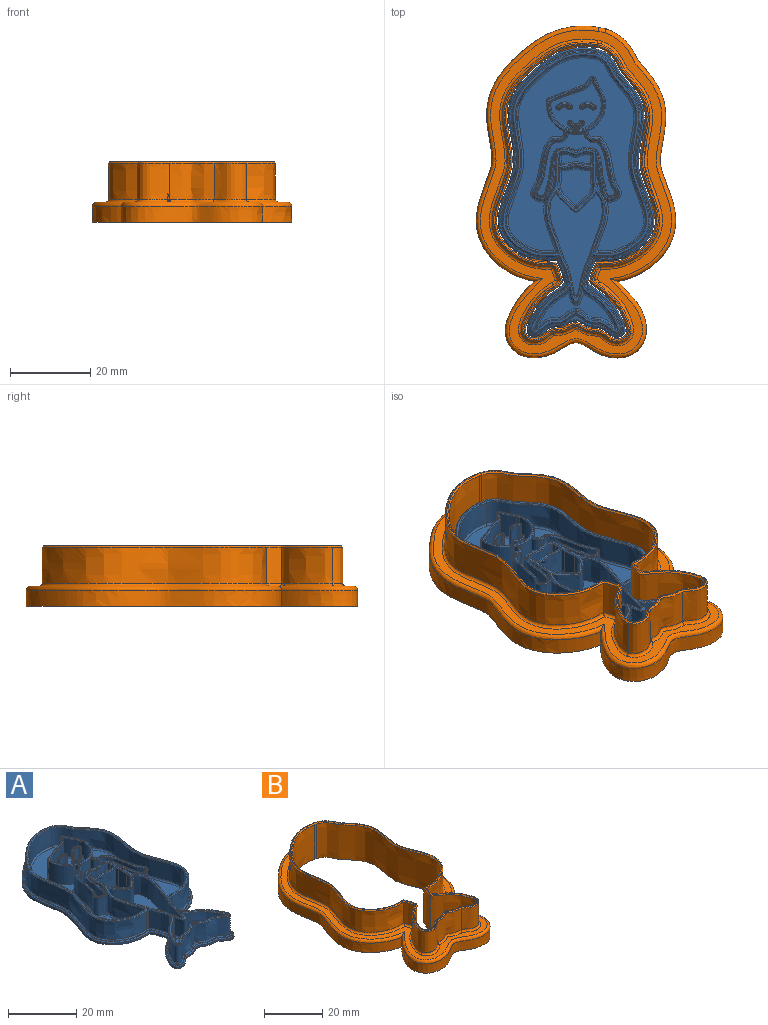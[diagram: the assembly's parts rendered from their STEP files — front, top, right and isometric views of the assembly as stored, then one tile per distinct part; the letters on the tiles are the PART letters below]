
ASSEMBLY  parts=2 mates=1
PART A: 305 faces, bbox 39.4x72.6x8.6 mm
  f0: plane 70.17x36.96mm, normal (0,0,1), area 142.6mm2, adj f242,f245,f246,f251,f252,f257,f262,f263
  f1: plane 12.52x11.75mm, normal (0,0,1), area 76.7mm2, adj f139,f140,f141,f142,f145,f146,f147,f148
  f2: plane 71.4x38.2mm, normal (0,0,1), area 60.9mm2, adj f98,f100,f101,f102,f103,f104,f105,f106
  f3: extruded ~5.41x1.93mm, area 3.7mm2, adj f4,f8,f9,f112
  f4: extruded ~52.46x14.48mm, area 43.8mm2, adj f3,f5,f9,f114
  f5: plane 0.65x0.51mm, normal (0.21,0.98,0), area 0.3mm2, adj f4,f6,f9,f115
  f6: extruded ~52.96x24.58mm, area 50.2mm2, adj f5,f7,f9,f113
  f7: extruded ~5.44x1.91mm, area 3.8mm2, adj f6,f8,f9,f111
  f8: extruded ~24.23x13.75mm, area 38.4mm2, adj f3,f7,f9,f110
  f9: plane 72.05x38.76mm, normal (0,0,-1), area 1871mm2, adj f3,f4,f5,f6,f7,f8
  f10: extruded ~6.25x3.82mm, area 54mm2, adj f11,f75,f123,f304
  f11: extruded ~6.25x1.11mm, area 8.5mm2, adj f10,f12,f121,f303
  f12: extruded ~20.45x9mm, area 320.2mm2, adj f11,f75,f116,f117,f118,f119,f120,f301
  f13: extruded ~9.98x6.75mm, area 96mm2, adj f68,f82,f288
  f14: extruded ~8.21x6.25mm, area 52.4mm2, adj f15,f69,f131,f286
  f15: plane 6.25x1mm, normal (-1,0,0), area 6.3mm2, adj f14,f16,f129,f287
  f16: extruded ~6.25x3.42mm, area 21.4mm2, adj f15,f17,f127,f285
  f17: extruded ~8.51x6.25mm, area 91.1mm2, adj f16,f18,f124,f125,f126,f283
  f18: extruded ~6.25x3.52mm, area 22mm2, adj f17,f69,f128,f282
  f19: extruded ~8.22x6.25mm, area 52.2mm2, adj f20,f70,f136,f277
  f20: extruded ~6.25x2.57mm, area 16.1mm2, adj f19,f21,f135,f278
  f21: extruded ~8.42x6.25mm, area 55.2mm2, adj f20,f22,f133,f280
  f22: extruded ~6.25x1.16mm, area 7.3mm2, adj f21,f70,f132,f281
  f23: cylinder r=7.36mm len=6.45mm, axis (0,0,-1), area 30.8mm2, adj f24,f71,f186,f255
  f24: extruded ~6.45x2.13mm, area 16.7mm2, adj f23,f25,f184,f260
  f25: plane 6.45x0.56mm, normal (-0.36,-0.93,0), area 3.9mm2, adj f24,f26,f182,f264
  f26: extruded ~13.82x6.45mm, area 114.8mm2, adj f25,f27,f180,f268
  f27: extruded ~6.45x0.57mm, area 4.2mm2, adj f26,f28,f178,f272
  f28: extruded ~10.59x6.45mm, area 71mm2, adj f27,f176,f204,f276
  f29: extruded ~8.97x6.45mm, area 60.4mm2, adj f173,f201,f204,f271
  f30: extruded ~10.56x6.45mm, area 70.8mm2, adj f31,f177,f201,f263
  f31: extruded ~6.45x0.61mm, area 4.4mm2, adj f30,f32,f179,f259
  f32: extruded ~13.82x6.45mm, area 114.7mm2, adj f31,f33,f181,f254
  f33: plane 6.45x0.56mm, normal (0.36,-0.93,0), area 3.9mm2, adj f32,f71,f183,f248
  f34: extruded ~6.75x0.44mm, area 3mm2, adj f72,f78,f207,f234
  f35: cylinder r=7.36mm len=7.47mm, axis (0,0,-1), area 61.4mm2, adj f36,f78,f207,f243
  f36: extruded ~6.75x1.9mm, area 15.2mm2, adj f35,f37,f78,f194,f247
  f37: extruded ~15.41x6.73mm, area 124.5mm2, adj f36,f38,f194,f253
  f38: extruded ~10.1x6.25mm, area 69mm2, adj f37,f39,f196,f258
  f39: extruded ~6.74x3.04mm, area 19.8mm2, adj f38,f40,f196,f252
  f40: extruded ~6.74x3.26mm, area 21.6mm2, adj f39,f41,f196,f198,f246
  f41: extruded ~16.84x6.25mm, area 111.4mm2, adj f40,f42,f198,f242
  f42: extruded ~6.25x1.04mm, area 6.5mm2, adj f41,f43,f200,f245
  f43: extruded ~48.95x22.38mm, area 437.8mm2, adj f42,f44,f199,f251
  f44: extruded ~48.58x12.27mm, area 379.6mm2, adj f43,f45,f197,f257
  f45: extruded ~6.25x1.02mm, area 6.4mm2, adj f44,f46,f195,f262
  f46: extruded ~16.67x6.25mm, area 110.3mm2, adj f45,f47,f193,f266
  f47: extruded ~6.74x3.26mm, area 21.6mm2, adj f46,f48,f192,f193,f270
  f48: extruded ~6.74x3.04mm, area 19.8mm2, adj f47,f49,f192,f274
  f49: extruded ~10.1x6.25mm, area 69.1mm2, adj f48,f50,f192,f273
  f50: extruded ~15.41x6.73mm, area 124.5mm2, adj f49,f51,f191,f269
  f51: extruded ~6.75x1.9mm, area 15.2mm2, adj f50,f52,f78,f191,f265
  f52: cylinder r=7.36mm len=8.12mm, axis (0,0,-1), area 65.9mm2, adj f51,f53,f78,f261
  f53: extruded ~6.75x0.98mm, area 7.1mm2, adj f52,f54,f78,f256
  f54: extruded ~6.75x3.75mm, area 28.3mm2, adj f53,f78,f208,f250
  f55: cylinder r=6.56mm len=13.12mm, axis (0,0,-1), area 144.3mm2, adj f56,f73,f190,f236
  f56: extruded ~10.63x6.45mm, area 80.2mm2, adj f55,f57,f189,f240
  f57: extruded ~6.45x4.08mm, area 29.3mm2, adj f56,f73,f187,f239
  f58: extruded ~50.95x23.41mm, area 470.6mm2, adj f59,f74,f109,f295
  f59: extruded ~6.4x1.05mm, area 6.7mm2, adj f58,f60,f107,f297
  f60: extruded ~6.46x6.4mm, area 44mm2, adj f59,f61,f105,f299
  f61: plane 6.45x0.02mm, normal (-1,0,0), area 0mm2, adj f60,f62,f103,f105
  f62: extruded ~6.4x1.13mm, area 8.9mm2, adj f61,f63,f103,f298
  f63: extruded ~21.69x11.47mm, area 332.1mm2, adj f62,f64,f98,f99,f101,f296
  f64: extruded ~6.4x1.16mm, area 9mm2, adj f63,f65,f100,f294
  f65: extruded ~6.63x6.4mm, area 45.2mm2, adj f64,f66,f102,f292
  f66: extruded ~6.4x1.03mm, area 6.6mm2, adj f65,f67,f104,f290
  f67: extruded ~50.5x13.09mm, area 409.1mm2, adj f66,f74,f106,f291
  f68: extruded ~25.64x13.13mm, area 372.4mm2, adj f13,f82,f289
  f69: extruded ~6.25x1mm, area 6.2mm2, adj f14,f18,f130,f284
  f70: plane 6.25x1.42mm, normal (-1,0,0), area 8.9mm2, adj f19,f22,f134,f279
  f71: extruded ~6.45x2.13mm, area 16.7mm2, adj f23,f33,f185,f249
  f72: extruded ~9.24x6.75mm, area 71mm2, adj f34,f78,f209,f237
  f73: extruded ~6.45x0.8mm, area 5.6mm2, adj f55,f57,f188,f235
  f74: plane 6.4x0.39mm, normal (0.21,0.98,0), area 2.5mm2, adj f58,f67,f108,f293
  f75: extruded ~6.25x1.12mm, area 8.6mm2, adj f10,f12,f122,f302
  f76: plane 30.71x21.28mm, normal (0,0,1), area 34mm2, adj f234,f235,f236,f237,f238,f239,f240,f241
  f77: plane 18.66x7.91mm, normal (0,0,1), area 52.3mm2, adj f116,f119,f120,f121,f122,f123
  f78: plane 47.99x33.76mm, normal (0,0,1), area 643mm2, adj f34,f35,f36,f51,f52,f53,f54,f72
  f79: plane 19.34x15.39mm, normal (0,0,1), area 54.9mm2, adj f173,f174,f175,f176,f177,f178,f179,f180
  f80: plane 7.47x2.21mm, normal (0,0,1), area 12.8mm2, adj f132,f133,f134,f135,f136
  f81: plane 9.15x7.51mm, normal (0,0,1), area 51.6mm2, adj f125,f126,f127,f128,f129,f130,f131
  f82: plane 26.04x13.44mm, normal (0,0,1), area 171.7mm2, adj f13,f68
  f83: plane 6.45x0.19mm, normal (0.39,0.92,0), area 1.3mm2, adj f167,f168,f172,f232
  f84: cylinder r=1.38mm len=6.45mm, axis (0,0,-1), area 17.6mm2, adj f162,f168,f169,f228
  f85: plane 6.45x0.19mm, normal (-0.39,0.92,0), area 1.3mm2, adj f161,f162,f163,f227
  f86: cylinder r=2.18mm len=6.45mm, axis (0,0,-1), area 28.3mm2, adj f161,f166,f167,f231
  f87: plane 3.28x1.05mm, normal (0,0,1), area 1.1mm2, adj f226,f227,f228,f229,f230,f231,f232,f233
  f88: plane 6.45x0.17mm, normal (-0.57,-0.82,0), area 1.3mm2, adj f154,f157,f160,f215
  f89: cylinder r=1.53mm len=6.45mm, axis (0,0,-1), area 16.5mm2, adj f149,f154,f155,f216
  f90: plane 6.45x0.17mm, normal (0.51,-0.86,0), area 1.3mm2, adj f149,f150,f151,f212
  f91: cylinder r=2.33mm len=6.45mm, axis (0,0,-1), area 25.7mm2, adj f151,f156,f157,f211
  f92: plane 3.16x0.95mm, normal (0,0,1), area 1mm2, adj f210,f211,f212,f213,f214,f215,f216,f217
  f93: cylinder r=1.53mm len=6.45mm, axis (0,0,-1), area 16.5mm2, adj f143,f144,f148,f224
  f94: plane 6.45x0.17mm, normal (0.57,-0.82,0), area 1.3mm2, adj f138,f144,f145,f220
  f95: cylinder r=2.33mm len=6.45mm, axis (0,0,-1), area 25.7mm2, adj f137,f138,f139,f219
  f96: plane 6.45x0.17mm, normal (-0.51,-0.86,0), area 1.3mm2, adj f137,f142,f143,f223
  f97: plane 3.16x0.95mm, normal (0,0,1), area 1mm2, adj f218,f219,f220,f221,f222,f223,f224,f225
  f98: bspline ~12x11.61mm, area 14.7mm2, adj f2,f63,f99,f100
  f99: bspline ~0.35x0.35mm, area 0mm2, adj f63,f98,f101
  f100: bspline ~1.71x1.28mm, area 0.7mm2, adj f2,f64,f98,f102
  f101: bspline ~12x11.61mm, area 15mm2, adj f2,f63,f99,f103
  f102: bspline ~7.49x2.86mm, area 3.7mm2, adj f2,f65,f100,f104
  f103: bspline ~1.89x1.5mm, area 0.7mm2, adj f2,f61,f62,f101,f105
  f104: bspline ~1.51x0.47mm, area 0.5mm2, adj f2,f66,f102,f106
  f105: bspline ~7.79x3mm, area 3.7mm2, adj f2,f60,f61,f103,f107
  f106: bspline ~51.37x27.17mm, area 35.3mm2, adj f2,f67,f104,f108
  f107: bspline ~1.49x0.41mm, area 0.5mm2, adj f2,f59,f105,f109
  f108: cylinder r=0.35mm len=0.5mm, axis (0.98,-0.21,0), area 0.2mm2, adj f2,f74,f106,f109
  f109: bspline ~51.69x25.19mm, area 40.7mm2, adj f2,f58,f107,f108
  f110: bspline ~24.34x14.17mm, area 32.3mm2, adj f2,f8,f111,f112
  f111: bspline ~7.78x3.04mm, area 3.3mm2, adj f2,f7,f110,f113
  f112: bspline ~7.02x2.7mm, area 3.3mm2, adj f2,f3,f110,f114
  f113: bspline ~52.99x25.08mm, area 42.3mm2, adj f2,f6,f111,f115
  f114: bspline ~52.57x15.23mm, area 36.7mm2, adj f2,f4,f112,f115
  f115: cylinder r=0.35mm len=0.58mm, axis (0.98,-0.21,0), area 0.3mm2, adj f2,f5,f113,f114
  f116: bspline ~20.48x5.28mm, area 17mm2, adj f12,f77,f117,f118
  f117: bspline ~1.14x0.93mm, area 0.3mm2, adj f12,f116,f119
  f118: bspline ~1.14x0.93mm, area 0.4mm2, adj f12,f116,f120
  f119: bspline ~9.42x8.61mm, area 9mm2, adj f12,f77,f117,f121
  f120: bspline ~9.3x8.39mm, area 9mm2, adj f12,f77,f118,f122
  f121: bspline ~1.82x1.52mm, area 0.7mm2, adj f11,f77,f119,f123
  f122: bspline ~3.59x3.28mm, area 0.7mm2, adj f75,f77,f120,f123
  f123: bspline ~5.07x4.45mm, area 6.3mm2, adj f10,f77,f121,f122
  f124: bspline ~0.59x0.5mm, area 0.1mm2, adj f17,f125,f126
  f125: bspline ~6.93x4.44mm, area 5.3mm2, adj f17,f81,f124,f127
  f126: bspline ~5.64x4.48mm, area 5.3mm2, adj f17,f81,f124,f128
  f127: bspline ~4.71x0.66mm, area 2.7mm2, adj f16,f81,f125,f129
  f128: bspline ~4.88x0.66mm, area 2.8mm2, adj f18,f81,f126,f130
  f129: cylinder r=0.5mm len=1mm, axis (0,1,0), area 0.5mm2, adj f15,f81,f127,f131
  f130: bspline ~1.26x0.51mm, area 0.5mm2, adj f69,f81,f128,f131
  f131: bspline ~8.99x1.05mm, area 6.2mm2, adj f14,f81,f129,f130
  f132: bspline ~1.76x0.7mm, area 0.8mm2, adj f22,f80,f133,f134
  f133: bspline ~8.83x1.25mm, area 6.6mm2, adj f21,f80,f132,f135
  f134: cylinder r=0.5mm len=1.48mm, axis (0,1,0), area 1mm2, adj f70,f80,f132,f136
  f135: bspline ~2.82x0.65mm, area 1.7mm2, adj f20,f80,f133,f136
  f136: bspline ~9.17x0.96mm, area 6.2mm2, adj f19,f80,f134,f135
  f137: cylinder r=0.3mm len=6.45mm, axis (0,0,-1), area 3.3mm2, adj f95,f96,f140,f221
  f138: cylinder r=0.3mm len=6.45mm, axis (0,0,-1), area 3.3mm2, adj f94,f95,f141,f218
  f139: torus R=2.63mm, axis (0,0,1), area 2mm2, adj f1,f95,f140,f141
  f140: torus R=0.6mm, axis (0,0,1), area 0.3mm2, adj f1,f137,f139,f142
  f141: torus R=0.6mm, axis (0,0,1), area 0.3mm2, adj f1,f138,f139,f145
  f142: cylinder r=0.3mm len=0.36mm, axis (-0.86,0.51,0), area 0.1mm2, adj f1,f96,f140,f146
  f143: cylinder r=0.3mm len=6.45mm, axis (0,0,-1), area 2.7mm2, adj f93,f96,f146,f225
  f144: cylinder r=0.3mm len=6.45mm, axis (0,0,-1), area 2.7mm2, adj f93,f94,f147,f222
  f145: cylinder r=0.3mm len=0.36mm, axis (-0.82,-0.57,0), area 0.1mm2, adj f1,f94,f141,f147
  f146: torus R=0.6mm, axis (0,0,1), area 0.3mm2, adj f1,f142,f143,f148
  f147: torus R=0.6mm, axis (0,0,1), area 0.3mm2, adj f1,f144,f145,f148
  f148: torus R=1.23mm, axis (0,0,1), area 1.1mm2, adj f1,f93,f146,f147
  f149: cylinder r=0.3mm len=6.45mm, axis (0,0,-1), area 2.7mm2, adj f89,f90,f152,f214
  f150: cylinder r=0.3mm len=0.36mm, axis (-0.86,-0.51,0), area 0.1mm2, adj f1,f90,f152,f153
  f151: cylinder r=0.3mm len=6.45mm, axis (0,0,-1), area 3.3mm2, adj f90,f91,f153,f210
  f152: torus R=0.6mm, axis (0,0,1), area 0.3mm2, adj f1,f149,f150,f155
  f153: torus R=0.6mm, axis (0,0,1), area 0.3mm2, adj f1,f150,f151,f156
  f154: cylinder r=0.3mm len=6.45mm, axis (0,0,-1), area 2.7mm2, adj f88,f89,f158,f217
  f155: torus R=1.23mm, axis (0,0,1), area 1.1mm2, adj f1,f89,f152,f158
  f156: torus R=2.63mm, axis (0,0,1), area 2mm2, adj f1,f91,f153,f159
  f157: cylinder r=0.3mm len=6.45mm, axis (0,0,-1), area 3.3mm2, adj f88,f91,f159,f213
  f158: torus R=0.6mm, axis (0,0,1), area 0.3mm2, adj f1,f154,f155,f160
  f159: torus R=0.6mm, axis (0,0,1), area 0.3mm2, adj f1,f156,f157,f160
  f160: cylinder r=0.3mm len=0.36mm, axis (-0.82,0.57,0), area 0.1mm2, adj f1,f88,f158,f159
  f161: cylinder r=0.3mm len=6.45mm, axis (0,0,-1), area 3.3mm2, adj f85,f86,f164,f229
  f162: cylinder r=0.3mm len=6.45mm, axis (0,0,-1), area 2.7mm2, adj f84,f85,f165,f226
  f163: cylinder r=0.3mm len=0.36mm, axis (0.92,0.39,0), area 0.1mm2, adj f1,f85,f164,f165
  f164: torus R=0.6mm, axis (0,0,1), area 0.3mm2, adj f1,f161,f163,f166
  f165: torus R=0.6mm, axis (0,0,1), area 0.3mm2, adj f1,f162,f163,f169
  f166: torus R=2.48mm, axis (0,0,1), area 2.2mm2, adj f1,f86,f164,f170
  f167: cylinder r=0.3mm len=6.45mm, axis (0,0,-1), area 3.3mm2, adj f83,f86,f170,f233
  f168: cylinder r=0.3mm len=6.45mm, axis (0,0,-1), area 2.7mm2, adj f83,f84,f171,f230
  f169: torus R=1.08mm, axis (0,0,1), area 1.2mm2, adj f1,f84,f165,f171
  f170: torus R=0.6mm, axis (0,0,1), area 0.3mm2, adj f1,f166,f167,f172
  f171: torus R=0.6mm, axis (0,0,1), area 0.3mm2, adj f1,f168,f169,f172
  f172: cylinder r=0.3mm len=0.36mm, axis (0.92,-0.39,0), area 0.1mm2, adj f1,f83,f170,f171
  f173: bspline ~9.92x1.06mm, area 4.4mm2, adj f29,f79,f174,f175,f203,f205
  f174: cylinder r=0.3mm len=0.2mm, axis (1,0,0), area 0mm2, adj f79,f173,f206
  f175: cylinder r=0.3mm len=0.2mm, axis (1,0,0), area 0mm2, adj f79,f173,f202
  f176: bspline ~13.6x4.17mm, area 5.3mm2, adj f28,f79,f178,f205,f206
  f177: bspline ~20.63x6.61mm, area 5.3mm2, adj f30,f79,f179,f202,f203
  f178: bspline ~1.05x0.75mm, area 0.3mm2, adj f27,f79,f176,f180
  f179: bspline ~0.87x0.65mm, area 0.3mm2, adj f31,f79,f177,f181
  f180: bspline ~13.83x6.11mm, area 8.2mm2, adj f26,f79,f178,f182
  f181: bspline ~13.82x6.45mm, area 8.2mm2, adj f32,f79,f179,f183
  f182: cylinder r=0.3mm len=0.77mm, axis (-0.93,0.36,0), area 0.3mm2, adj f25,f79,f180,f184
  f183: cylinder r=0.3mm len=0.77mm, axis (-0.93,-0.36,0), area 0.3mm2, adj f33,f79,f181,f185
  f184: bspline ~3.32x2.33mm, area 1.2mm2, adj f24,f79,f182,f186
  f185: bspline ~3.32x2.33mm, area 1.2mm2, adj f71,f79,f183,f186
  f186: torus R=7.66mm, axis (0,0,1), area 2.1mm2, adj f23,f79,f184,f185
  f187: bspline ~5.63x2.91mm, area 2mm2, adj f1,f57,f188,f189
  f188: bspline ~1.44x0.79mm, area 0.4mm2, adj f1,f73,f187,f190
  f189: bspline ~11.14x6.3mm, area 5.7mm2, adj f1,f56,f187,f190
  f190: torus R=6.26mm, axis (0,0,1), area 10.3mm2, adj f1,f55,f188,f189
  f191: bspline ~16.42x8.43mm, area 16.3mm2, adj f50,f51,f78,f192
  f192: bspline ~10.92x5.57mm, area 6.2mm2, adj f47,f48,f49,f78,f191,f193
  f193: bspline ~30.74x5.23mm, area 14.7mm2, adj f46,f47,f78,f192,f195
  f194: bspline ~16.44x9.14mm, area 16.3mm2, adj f36,f37,f78,f196
  f195: bspline ~1.36x0.6mm, area 0.6mm2, adj f45,f78,f193,f197
  f196: bspline ~10.95x5.58mm, area 6.2mm2, adj f38,f39,f40,f78,f194,f198
  f197: bspline ~48.66x25.3mm, area 47.3mm2, adj f44,f78,f195,f199
  f198: bspline ~23.14x3.86mm, area 14.8mm2, adj f40,f41,f78,f196,f200
  f199: bspline ~48.99x22.66mm, area 54.5mm2, adj f43,f78,f197,f200
  f200: bspline ~1.49x0.55mm, area 0.6mm2, adj f42,f78,f198,f199
  f201: cylinder r=1mm len=6.45mm, axis (0,0,-1), area 3.4mm2, adj f29,f30,f203,f267
  f202: bspline ~0.36x0.3mm, area 0mm2, adj f175,f177,f203
  f203: bspline ~0.45x0.45mm, area 0.1mm2, adj f173,f177,f201,f202
  f204: cylinder r=1mm len=6.45mm, axis (0,0,-1), area 3.4mm2, adj f28,f29,f205,f275
  f205: bspline ~0.48x0.45mm, area 0.1mm2, adj f173,f176,f204,f206
  f206: bspline ~0.36x0.3mm, area 0mm2, adj f174,f176,f205
  f207: cylinder r=1mm len=6.75mm, axis (0,0,-1), area 9.2mm2, adj f34,f35,f78,f238
  f208: cylinder r=1mm len=6.75mm, axis (0,0,-1), area 9.4mm2, adj f54,f78,f209,f244
  f209: cylinder r=1mm len=6.75mm, axis (0,0,-1), area 5mm2, adj f72,f78,f208,f241
  f210: cone r=0.05mm half-angle=45deg, axis (0,0,-1), area 0.1mm2, adj f92,f151,f211,f212
  f211: cone r=2.08mm half-angle=45deg, axis (0,0,-1), area 1.3mm2, adj f91,f92,f210,f213
  f212: plane 0.32x0.3mm, normal (0.36,-0.61,0.71), area 0.1mm2, adj f90,f92,f210,f214
  f213: cone r=0.05mm half-angle=45deg, axis (0,0,-1), area 0.1mm2, adj f92,f157,f211,f215
  f214: cone r=0.05mm half-angle=45deg, axis (0,0,-1), area 0.1mm2, adj f92,f149,f212,f216
  f215: plane 0.32x0.31mm, normal (-0.4,-0.58,0.71), area 0.1mm2, adj f88,f92,f213,f217
  f216: cone r=1.53mm half-angle=45deg, axis (0,0,1), area 1mm2, adj f89,f92,f214,f217
  f217: cone r=0.05mm half-angle=45deg, axis (0,0,-1), area 0.1mm2, adj f92,f154,f215,f216
  f218: cone r=0.05mm half-angle=45deg, axis (0,0,-1), area 0.1mm2, adj f97,f138,f219,f220
  f219: cone r=2.08mm half-angle=45deg, axis (0,0,-1), area 1.3mm2, adj f95,f97,f218,f221
  f220: plane 0.32x0.31mm, normal (0.4,-0.58,0.71), area 0.1mm2, adj f94,f97,f218,f222
  f221: cone r=0.05mm half-angle=45deg, axis (0,0,-1), area 0.1mm2, adj f97,f137,f219,f223
  f222: cone r=0.05mm half-angle=45deg, axis (0,0,-1), area 0.1mm2, adj f97,f144,f220,f224
  f223: plane 0.32x0.3mm, normal (-0.36,-0.61,0.71), area 0.1mm2, adj f96,f97,f221,f225
  f224: cone r=1.53mm half-angle=45deg, axis (0,0,1), area 1mm2, adj f93,f97,f222,f225
  f225: cone r=0.05mm half-angle=45deg, axis (0,0,-1), area 0.1mm2, adj f97,f143,f223,f224
  f226: cone r=0.05mm half-angle=45deg, axis (0,0,-1), area 0.1mm2, adj f87,f162,f227,f228
  f227: plane 0.31x0.29mm, normal (-0.28,0.65,0.71), area 0.1mm2, adj f85,f87,f226,f229
  f228: cone r=1.38mm half-angle=45deg, axis (0,0,1), area 1.1mm2, adj f84,f87,f226,f230
  f229: cone r=0.05mm half-angle=45deg, axis (0,0,-1), area 0.1mm2, adj f87,f161,f227,f231
  f230: cone r=0.05mm half-angle=45deg, axis (0,0,-1), area 0.1mm2, adj f87,f168,f228,f232
  f231: cone r=1.93mm half-angle=45deg, axis (0,0,-1), area 1.5mm2, adj f86,f87,f229,f233
  f232: plane 0.31x0.29mm, normal (0.28,0.65,0.71), area 0.1mm2, adj f83,f87,f230,f233
  f233: cone r=0.05mm half-angle=45deg, axis (0,0,-1), area 0.1mm2, adj f87,f167,f231,f232
  f234: bspline ~0.54x0.33mm, area 0.2mm2, adj f34,f76,f237,f238
  f235: bspline ~0.95x0.58mm, area 0.3mm2, adj f73,f76,f236,f239
  f236: cone r=6.56mm half-angle=45deg, axis (0,0,1), area 8.1mm2, adj f55,f76,f235,f240
  f237: bspline ~9.96x5.01mm, area 3.7mm2, adj f72,f76,f234,f241
  f238: cone r=0.75mm half-angle=45deg, axis (0,0,-1), area 0.4mm2, adj f76,f207,f234,f243
  f239: bspline ~5.2x2.68mm, area 1.7mm2, adj f57,f76,f235,f240,f244
  f240: bspline ~11.79x7.55mm, area 4.5mm2, adj f56,f76,f236,f239,f244
  f241: cone r=0.75mm half-angle=45deg, axis (0,0,-1), area 0.2mm2, adj f76,f209,f237,f244
  f242: bspline ~18.52x3.64mm, area 6.3mm2, adj f0,f41,f245,f246
  f243: cone r=7.11mm half-angle=45deg, axis (0,0,-1), area 3.2mm2, adj f35,f76,f238,f247
  f244: cone r=0.75mm half-angle=45deg, axis (0,0,-1), area 0.4mm2, adj f76,f208,f239,f240,f241,f250
  f245: bspline ~1.37x0.3mm, area 0.4mm2, adj f0,f42,f242,f251
  f246: bspline ~3.45x0.42mm, area 1.2mm2, adj f0,f40,f242,f252
  f247: bspline ~2.54x1.33mm, area 0.9mm2, adj f36,f76,f243,f253
  f248: plane 0.62x0.44mm, normal (0.26,-0.66,0.71), area 0.2mm2, adj f33,f76,f249,f254
  f249: bspline ~2.76x1.42mm, area 0.9mm2, adj f71,f76,f248,f255
  f250: bspline ~4.05x2.19mm, area 1.5mm2, adj f54,f76,f244,f256
  f251: bspline ~49.53x23.17mm, area 25mm2, adj f0,f43,f245,f257
  f252: bspline ~5.19x0.29mm, area 1.4mm2, adj f0,f39,f246,f258
  f253: bspline ~15.47x7.4mm, area 6.9mm2, adj f37,f76,f247,f258
  f254: bspline ~14.35x6.74mm, area 6.5mm2, adj f32,f76,f248,f259
  f255: cone r=7.11mm half-angle=45deg, axis (0,0,-1), area 1.8mm2, adj f23,f76,f249,f260
  f256: bspline ~1.15x0.66mm, area 0.4mm2, adj f53,f76,f250,f261
  f257: bspline ~49.73x14.25mm, area 21.5mm2, adj f0,f44,f251,f262
  f258: bspline ~12.61x3.74mm, area 4.2mm2, adj f38,f76,f252,f253,f263
  f259: bspline ~0.77x0.55mm, area 0.3mm2, adj f31,f76,f254,f263
  f260: bspline ~2.76x1.42mm, area 0.9mm2, adj f24,f76,f255,f264
  f261: cone r=7.11mm half-angle=45deg, axis (0,0,-1), area 3.4mm2, adj f52,f76,f256,f265
  f262: bspline ~1.35x0.36mm, area 0.4mm2, adj f0,f45,f257,f266
  f263: bspline ~10.65x2.73mm, area 3.9mm2, adj f0,f30,f76,f258,f259,f267
  f264: plane 0.62x0.44mm, normal (-0.26,-0.66,0.71), area 0.2mm2, adj f25,f76,f260,f268
  f265: bspline ~2.54x1.33mm, area 0.9mm2, adj f51,f76,f261,f269
  f266: bspline ~18.33x3.58mm, area 6.3mm2, adj f0,f46,f262,f270
  f267: cone r=0.75mm half-angle=45deg, axis (0,0,-1), area 0.2mm2, adj f0,f201,f263,f271
  f268: bspline ~14.35x6.75mm, area 6.5mm2, adj f26,f76,f264,f272
  f269: bspline ~15.47x7.42mm, area 6.9mm2, adj f50,f76,f265,f273
  f270: bspline ~3.28x0.4mm, area 1.2mm2, adj f0,f47,f266,f274
  f271: bspline ~9.83x1.05mm, area 3.3mm2, adj f0,f29,f267,f275
  f272: bspline ~0.73x0.54mm, area 0.2mm2, adj f27,f76,f268,f276
  f273: bspline ~12.62x3.74mm, area 4.2mm2, adj f49,f76,f269,f274,f276
  f274: bspline ~5.2x0.29mm, area 1.4mm2, adj f0,f48,f270,f273
  f275: cone r=0.75mm half-angle=45deg, axis (0,0,-1), area 0.2mm2, adj f0,f204,f271,f276
  f276: bspline ~10.68x2.74mm, area 3.9mm2, adj f0,f28,f76,f272,f273,f275
  f277: bspline ~9.57x0.73mm, area 3mm2, adj f0,f19,f278,f279
  f278: bspline ~3.2x0.41mm, area 1mm2, adj f0,f20,f277,f280
  f279: plane 1.61x0.25mm, normal (-0.71,0,0.71), area 0.5mm2, adj f0,f70,f277,f281
  f280: bspline ~9.68x1.04mm, area 3.2mm2, adj f0,f21,f278,f281
  f281: bspline ~1.37x0.37mm, area 0.4mm2, adj f0,f22,f279,f280
  f282: bspline ~3.52x0.42mm, area 1.2mm2, adj f0,f18,f283,f284
  f283: bspline ~9.01x5.75mm, area 5.3mm2, adj f0,f17,f282,f285
  f284: bspline ~1.43x0.26mm, area 0.4mm2, adj f0,f69,f282,f286
  f285: bspline ~3.42x0.42mm, area 1.2mm2, adj f0,f16,f283,f287
  f286: bspline ~9.71x0.82mm, area 3.1mm2, adj f0,f14,f284,f287
  f287: plane 1.37x0.25mm, normal (-0.71,0,0.71), area 0.4mm2, adj f0,f15,f285,f286
  f288: bspline ~10.31x5.43mm, area 5.1mm2, adj f0,f13,f289
  f289: bspline ~27.91x13.69mm, area 19.5mm2, adj f0,f68,f288
  f290: bspline ~1.3x0.36mm, area 0.4mm2, adj f0,f66,f291,f292
  f291: bspline ~51.2x14.76mm, area 22.4mm2, adj f0,f67,f290,f293
  f292: bspline ~7.77x2.89mm, area 2.6mm2, adj f0,f65,f290,f294
  f293: plane 0.44x0.33mm, normal (0.15,0.69,0.71), area 0.1mm2, adj f0,f74,f291,f295
  f294: bspline ~1.43x1.11mm, area 0.5mm2, adj f0,f64,f292,f296
  f295: bspline ~51.03x23.93mm, area 25.9mm2, adj f0,f58,f293,f297
  f296: bspline ~22.59x11.51mm, area 20.3mm2, adj f0,f63,f294,f298
  f297: bspline ~1.24x0.3mm, area 0.4mm2, adj f0,f59,f295,f299
  f298: bspline ~1.38x1.08mm, area 0.5mm2, adj f0,f62,f296,f300
  f299: bspline ~7.42x2.79mm, area 2.5mm2, adj f0,f60,f297,f300
  f300: plane 0.25x0.25mm, normal (-0.71,0,0.71), area 0mm2, adj f0,f298,f299
  f301: bspline ~21.03x9.65mm, area 17.6mm2, adj f0,f12,f302,f303
  f302: bspline ~1.94x1.32mm, area 0.6mm2, adj f0,f75,f301,f304
  f303: bspline ~1.87x1.28mm, area 0.6mm2, adj f0,f11,f301,f304
  f304: bspline ~5.04x3.68mm, area 3.2mm2, adj f0,f10,f302,f303
PART B: 61 faces, bbox 50x83.5x15.4 mm
  f0: extruded ~11.81x8.9mm, area 132.2mm2, adj f1,f10,f31,f46
  f1: extruded ~8.9x1.17mm, area 13.6mm2, adj f0,f2,f30,f44
  f2: extruded ~8.9x3.68mm, area 34.8mm2, adj f1,f3,f32,f43
  f3: extruded ~55.75x26mm, area 720.7mm2, adj f2,f4,f34,f45
  f4: plane 8.9x0.87mm, normal (0.21,0.98,0), area 7.9mm2, adj f3,f5,f36,f47
  f5: extruded ~55.19x15.01mm, area 625.8mm2, adj f4,f6,f38,f49
  f6: extruded ~8.9x3.6mm, area 34.1mm2, adj f5,f7,f40,f50
  f7: extruded ~8.9x1.03mm, area 11.7mm2, adj f6,f8,f42,f52
  f8: extruded ~12.34x8.9mm, area 136.9mm2, adj f7,f9,f41,f54
  f9: extruded ~8.9x8.05mm, area 86.9mm2, adj f8,f11,f39,f53
  f10: extruded ~8.9x7.9mm, area 86.5mm2, adj f0,f12,f33,f48
  f11: extruded ~11.05x8.9mm, area 103.8mm2, adj f9,f12,f37,f51
  f12: plane 8.9x0mm, normal (0.2,-0.98,0), area 0mm2, adj f10,f11,f35
  f13: extruded ~14.65x4.9mm, area 76.5mm2, adj f14,f18,f20,f59
  f14: extruded ~53.24x14.65mm, area 999.5mm2, adj f13,f15,f20,f60
  f15: plane 14.65x0.61mm, normal (-0.21,-0.98,0), area 9.1mm2, adj f14,f16,f20,f58
  f16: extruded ~53.76x24.99mm, area 1146.1mm2, adj f15,f17,f20,f56
  f17: extruded ~14.65x4.95mm, area 77.1mm2, adj f16,f18,f20,f55
  f18: extruded ~25.07x14.65mm, area 878.3mm2, adj f13,f17,f20,f57
  f19: plane 74.57x41.4mm, normal (0,0,1), area 68.4mm2, adj f43,f44,f45,f46,f47,f48,f49,f50
  f20: plane 83.04x49.56mm, normal (0,0,-1), area 1141.3mm2, adj f13,f14,f15,f16,f17,f18,f21,f22
  f21: extruded ~35.01x19.03mm, area 293.6mm2, adj f20,f22,f24,f29
  f22: extruded ~63.47x30.38mm, area 354.9mm2, adj f20,f21,f23,f28
  f23: plane 4x1.88mm, normal (0.21,0.98,0), area 7.7mm2, adj f20,f22,f24,f26
  f24: extruded ~62.73x17.21mm, area 305.2mm2, adj f20,f21,f23,f27
  f25: plane 80.55x47.57mm, normal (0,0,1), area 514.9mm2, adj f26,f27,f28,f29,f30,f31,f32,f33
  f26: cylinder r=1mm len=2.09mm, axis (-0.98,0.21,0), area 2.9mm2, adj f23,f25,f27,f28
  f27: bspline ~63.18x17.93mm, area 120.2mm2, adj f24,f25,f26,f29
  f28: bspline ~64.4x31.01mm, area 139.5mm2, adj f22,f25,f26,f29
  f29: bspline ~35.13x20.95mm, area 115.8mm2, adj f21,f25,f27,f28
  f30: bspline ~2.03x1.78mm, area 1.5mm2, adj f1,f25,f31,f32
  f31: bspline ~17.15x10.25mm, area 17.9mm2, adj f0,f25,f30,f33
  f32: bspline ~4.76x2.28mm, area 4mm2, adj f2,f25,f30,f34
  f33: bspline ~9.78x3.69mm, area 13mm2, adj f10,f25,f31,f35
  f34: bspline ~57.29x27.78mm, area 96mm2, adj f3,f25,f32,f36
  f35: cylinder r=0.75mm len=0.75mm, axis (-0.98,-0.2,0), area 0mm2, adj f12,f25,f33,f37
  f36: cylinder r=0.75mm len=1.12mm, axis (0.98,-0.21,0), area 1.1mm2, adj f4,f25,f34,f38
  f37: bspline ~13.24x2.76mm, area 13.6mm2, adj f11,f25,f35,f39
  f38: bspline ~56.82x16.16mm, area 83.2mm2, adj f5,f25,f36,f40
  f39: bspline ~11.14x5.49mm, area 12mm2, adj f9,f25,f37,f41
  f40: bspline ~4.53x2.24mm, area 3.9mm2, adj f6,f25,f38,f42
  f41: bspline ~15.48x11.22mm, area 18.5mm2, adj f8,f25,f39,f42
  f42: bspline ~1.91x1.7mm, area 1.2mm2, adj f7,f25,f40,f41
  f43: bspline ~4.62x1.89mm, area 2.1mm2, adj f2,f19,f44,f45
  f44: bspline ~1.61x1.47mm, area 0.8mm2, adj f1,f19,f43,f46
  f45: bspline ~55.8x26.9mm, area 39.9mm2, adj f3,f19,f43,f47
  f46: bspline ~11.81x8.21mm, area 7.3mm2, adj f0,f19,f44,f48
  f47: plane 0.92x0.52mm, normal (0.15,0.69,0.71), area 0.4mm2, adj f4,f19,f45,f49
  f48: bspline ~7.9x2.66mm, area 4.7mm2, adj f10,f19,f46,f51
  f49: bspline ~55.86x18.79mm, area 34.5mm2, adj f5,f19,f47,f50
  f50: bspline ~4.56x1.91mm, area 2mm2, adj f6,f19,f49,f52
  f51: bspline ~11.19x2.03mm, area 5.8mm2, adj f11,f19,f48,f53
  f52: bspline ~1.46x1.3mm, area 0.7mm2, adj f7,f19,f50,f54
  f53: bspline ~8.05x2.78mm, area 4.7mm2, adj f9,f19,f51,f54
  f54: bspline ~12.34x8.42mm, area 7.5mm2, adj f8,f19,f52,f53
  f55: bspline ~5.51x2.21mm, area 2.5mm2, adj f17,f19,f56,f57
  f56: bspline ~54.49x26.21mm, area 38.9mm2, adj f16,f19,f55,f58
  f57: bspline ~25.94x16.07mm, area 30.4mm2, adj f18,f19,f55,f59
  f58: plane 0.71x0.48mm, normal (-0.15,-0.69,0.71), area 0.3mm2, adj f15,f19,f56,f60
  f59: bspline ~5.46x2.23mm, area 2.5mm2, adj f13,f19,f57,f60
  f60: bspline ~54.61x18.5mm, area 33.8mm2, adj f14,f19,f58,f59
PLACE A t=(-4.17,-9.96,4.69)mm
PLACE B t=(-4.16,-9.94,4.69)mm
MATE fastened A.f9 <-> B.f20  axis (0,0,-1) through (-4.13,9.58,4.69)mm
